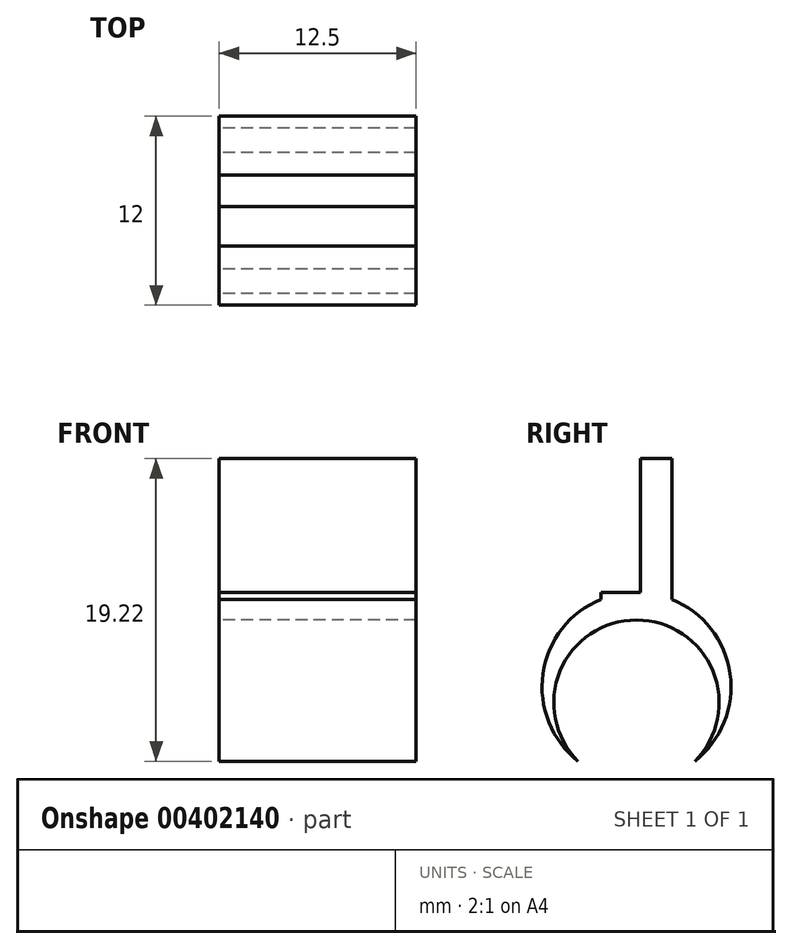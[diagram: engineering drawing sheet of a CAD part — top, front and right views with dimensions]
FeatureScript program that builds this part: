
annotation { "Feature Type Name" : "Feature", "Feature Type Description" : "" }
export const myFeature = defineFeature(function(context is Context, id is Id, definition is map)
    precondition{}
    {
        {
            var Q0;
            Q0=qCreatedBy(makeId("Top.planeOp"),FACE);
            var sketch = newSketch(context, id + "F0", { "sketchPlane" : qUnion([Q0])});
            skLineSegment(sketch, "E0.bottom", {"start": v(-6.25, 2.25) * mm, "end": v(6.25, 2.25) * mm});
            skLineSegment(sketch, "E0.top", {"start": v(-6.25, -2.25) * mm, "end": v(6.25, -2.25) * mm});
            skLineSegment(sketch, "E0.left", {"start": v(-6.25, 2.25) * mm, "end": v(-6.25, -2.25) * mm});
            skLineSegment(sketch, "E0.right", {"start": v(6.25, 2.25) * mm, "end": v(6.25, -2.25) * mm});
            skPoint(sketch, "E0.middle", {"position": v(0, 0) * mm});
            skSolve(sketch);
        }
        {
            var Q0;
            Q0 = qSketchRegion(id + "F0", true);
            extrude(context, id + "F1", {"entities" : qUnion([Q0]), "depth" : 0.5 * mm});
        }
        {
            var Q0;
            Q0=makeQuery(id+"F1.opExtrude","CAP_FACE",FACE,{"disambiguationData":[OSD([sQuery(id+"F0.wireOp",EDGE,"E0.bottom"),sQuery(id+"F0.wireOp",EDGE,"E0.top"),sQuery(id+"F0.wireOp",EDGE,"E0.left"),sQuery(id+"F0.wireOp",EDGE,"E0.right")])],"isStart":false});
            var sketch = newSketch(context, id + "F2", { "sketchPlane" : qUnion([Q0])});
            skLineSegment(sketch, "E1.bottom", {"start": v(-6.25, 2.25) * mm, "end": v(6.25, 2.25) * mm});
            skLineSegment(sketch, "E1.top", {"start": v(-6.25, 0.25) * mm, "end": v(6.25, 0.25) * mm});
            skLineSegment(sketch, "E1.left", {"start": v(-6.25, 2.25) * mm, "end": v(-6.25, 0.25) * mm});
            skLineSegment(sketch, "E1.right", {"start": v(6.25, 2.25) * mm, "end": v(6.25, 0.25) * mm});
            skSolve(sketch);
        }
        {
            var Q0;
            Q0 = qSketchRegion(id + "F2", true);
            extrude(context, id + "F3", {"entities" : qUnion([Q0]), "operationType" : NewBodyOperationType.ADD, "depth" : 8.5 * mm});
        }
        {
            var Q0;
            Q0=makeQuery(id+"F3.boolean.opBoolean","MERGE",FACE,{"derivedFrom":[makeQuery(id+"F1.opExtrude","SWEPT_FACE",FACE,{"disambiguationData":[OSD([sQuery(id+"F0.wireOp",EDGE,"E0.left")])]}),makeQuery(id+"F3.opExtrude","SWEPT_FACE",FACE,{"disambiguationData":[OSD([sQuery(id+"F2.wireOp",EDGE,"E1.left")])]})]});
            var sketch = newSketch(context, id + "F4", { "sketchPlane" : qUnion([Q0])});
            skCircle(sketch, "E2", {"center": v(0, -5.5) * mm, "radius": 6 * mm});
            skCircle(sketch, "E3", {"center": v(0, -6.5) * mm, "radius": 5.25 * mm});
            skSolve(sketch);
        }
        {
            var Q0;
            {var subQ4=sQuery(id+"F0.wireOp",EDGE,"E0.left");var subQ7=makeQuery(id+"F1.opExtrude","CAP_EDGE",EDGE,{"disambiguationData":[OSD([subQ4])],"isStart":true});Q0=makeQuery(id+"F4.imprint","IMPRINT",FACE,{"disambiguationData":[TD([[makeQuery(id+"F4.imprint","IMPRINT",EDGE,{"derivedFrom":subQ7}),-1.0]])]});}
            extrude(context, id + "F5", {"entities" : qUnion([Q0]), "operationType" : NewBodyOperationType.ADD, "oppositeDirection" : true, "depth" : 12.5 * mm});
        }
    });
